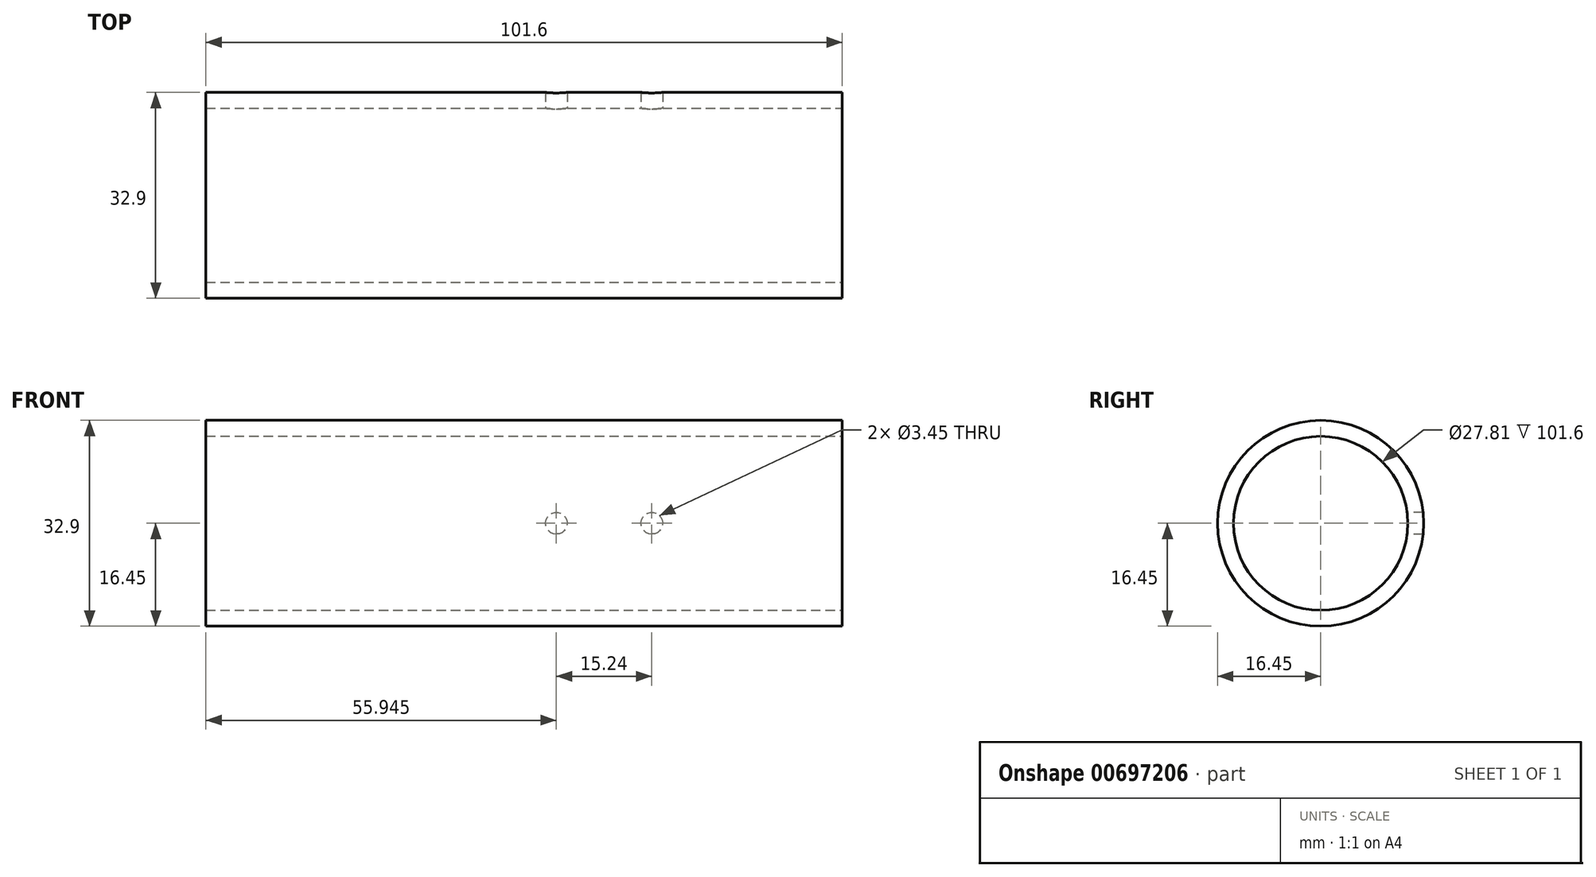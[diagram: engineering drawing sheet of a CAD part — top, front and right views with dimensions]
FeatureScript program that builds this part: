
annotation { "Feature Type Name" : "Feature", "Feature Type Description" : "" }
export const myFeature = defineFeature(function(context is Context, id is Id, definition is map)
    precondition{}
    {
        {
            var Q0;
            Q0=qCreatedBy(makeId("Right.planeOp"),FACE);
            var sketch = newSketch(context, id + "F0", { "sketchPlane" : qUnion([Q0])});
            skCircle(sketch, "E0", {"center": v(0, 0) * mm, "radius": 16.45 * mm});
            skSolve(sketch);
        }
        {
            var Q0;
            Q0=makeQuery(id+"F0.imprint","IMPRINT",FACE,{"disambiguationData":[TD([[makeQuery(id+"F0.imprint","IMPRINT",EDGE,{"derivedFrom":sQuery(id+"F0.wireOp",EDGE,"E0")}),1.0]])]});
            extrude(context, id + "F1", {"entities" : qUnion([Q0]), "depth" : 101.6 * mm, "offsetDistance" : 25.4 * mm});
        }
        {
            var Q0;
            Q0=makeQuery(id+"F1.opExtrude","CAP_FACE",FACE,{"disambiguationData":[OSD([sQuery(id+"F0.wireOp",EDGE,"E0")])],"isStart":false});
            var sketch = newSketch(context, id + "F2", { "sketchPlane" : qUnion([Q0])});
            skLineSegment(sketch, "E1", {"start": v(-16.45, 0) * mm, "end": v(0, 0) * mm});
            skCircle(sketch, "E2", {"center": v(0, 0) * mm, "radius": 13.9 * mm});
            skLineSegment(sketch, "E3", {"start": v(13.9, 0) * mm, "end": v(16.45, 0) * mm});
            skSolve(sketch);
        }
        {
            var Q0;
            Q0=qCreatedBy(makeId("Front.planeOp"),FACE);
            var sketch = newSketch(context, id + "F3", { "sketchPlane" : qUnion([Q0])});
            skLineSegment(sketch, "E4", {"start": v(96.58, 0) * mm, "end": v(71.18, 0) * mm});
            skLineSegment(sketch, "E5", {"start": v(71.18, 0) * mm, "end": v(55.94, 0) * mm});
            skLineSegment(sketch, "E6", {"start": v(55.94, 0) * mm, "end": v(0, 0) * mm});
            skSolve(sketch);
        }
        {
            var Q0;
            {var subQ0=sQuery(id+"F2.wireOp",EDGE,"E2");var subQ1=makeQuery(id+"F2.imprint","INTERSECT",VERTEX,{"derivedFrom":[subQ0,sQuery(id+"F2.wireOp",EDGE,"E3")]});Q0=makeQuery(id+"F2.imprint","IMPRINT",FACE,{"disambiguationData":[TD([[makeQuery(id+"F2.imprint","IMPRINT",EDGE,{"disambiguationData":[TD([[subQ1,-1.0]])],"derivedFrom":subQ0}),1.0]])]});}
            extrude(context, id + "F4", {"entities" : qUnion([Q0]), "operationType" : NewBodyOperationType.REMOVE, "endBound" : BoundingType.THROUGH_ALL, "oppositeDirection" : true, "depth" : 25.4 * mm, "offsetDistance" : 25.4 * mm});
        }
        {
            var Q0;
            Q0=sQuery(id+"F3.wireOp",VERTEX,"E5.start");
            var Q1;
            Q1=makeQuery(id+"F1.opExtrude","SWEPT_BODY",BODY,{"disambiguationData":[OSD([sQuery(id+"F0.wireOp",EDGE,"E0")])]});
            hole(context, id + "F5", {"style" : HoleStyle.SIMPLE, "endStyle" : HoleEndStyle.THROUGH, "standardTappedOrClearance" : lookupTablePath({ "standard" : "ANSI", "engagement" : "75%", "pitch" : "32 tpi", "size" : "#8", "type" : "Tapped" }), "standardBlindInLast" : lookupTablePath({ "standard" : "ANSI", "engagement" : "75%", "pitch" : "32 tpi", "size" : "#8", "type" : "Tapped" }), "holeDiameter" : 3.45 * mm, "majorDiameter" : 4.17 * mm, "showTappedDepth" : true, "isTappedThrough" : true, "tappedDepth" : 12.7 * mm, "tapClearance" : 3, "locations" : qUnion([Q0]), "scope" : qUnion([Q1])});
        }
        {
            var Q0;
            Q0=sQuery(id+"F3.wireOp",VERTEX,"E5.end");
            var Q1;
            Q1=makeQuery(id+"F1.opExtrude","SWEPT_BODY",BODY,{"disambiguationData":[OSD([sQuery(id+"F0.wireOp",EDGE,"E0")])]});
            hole(context, id + "F6", {"style" : HoleStyle.SIMPLE, "endStyle" : HoleEndStyle.THROUGH, "standardTappedOrClearance" : lookupTablePath({ "standard" : "ANSI", "engagement" : "75%", "pitch" : "32 tpi", "size" : "#8", "type" : "Tapped" }), "standardBlindInLast" : lookupTablePath({ "standard" : "ANSI", "engagement" : "75%", "pitch" : "32 tpi", "size" : "#8", "type" : "Tapped" }), "holeDiameter" : 3.45 * mm, "majorDiameter" : 4.17 * mm, "showTappedDepth" : true, "isTappedThrough" : true, "tappedDepth" : 12.7 * mm, "tapClearance" : 3, "locations" : qUnion([Q0]), "scope" : qUnion([Q1])});
        }
    });
